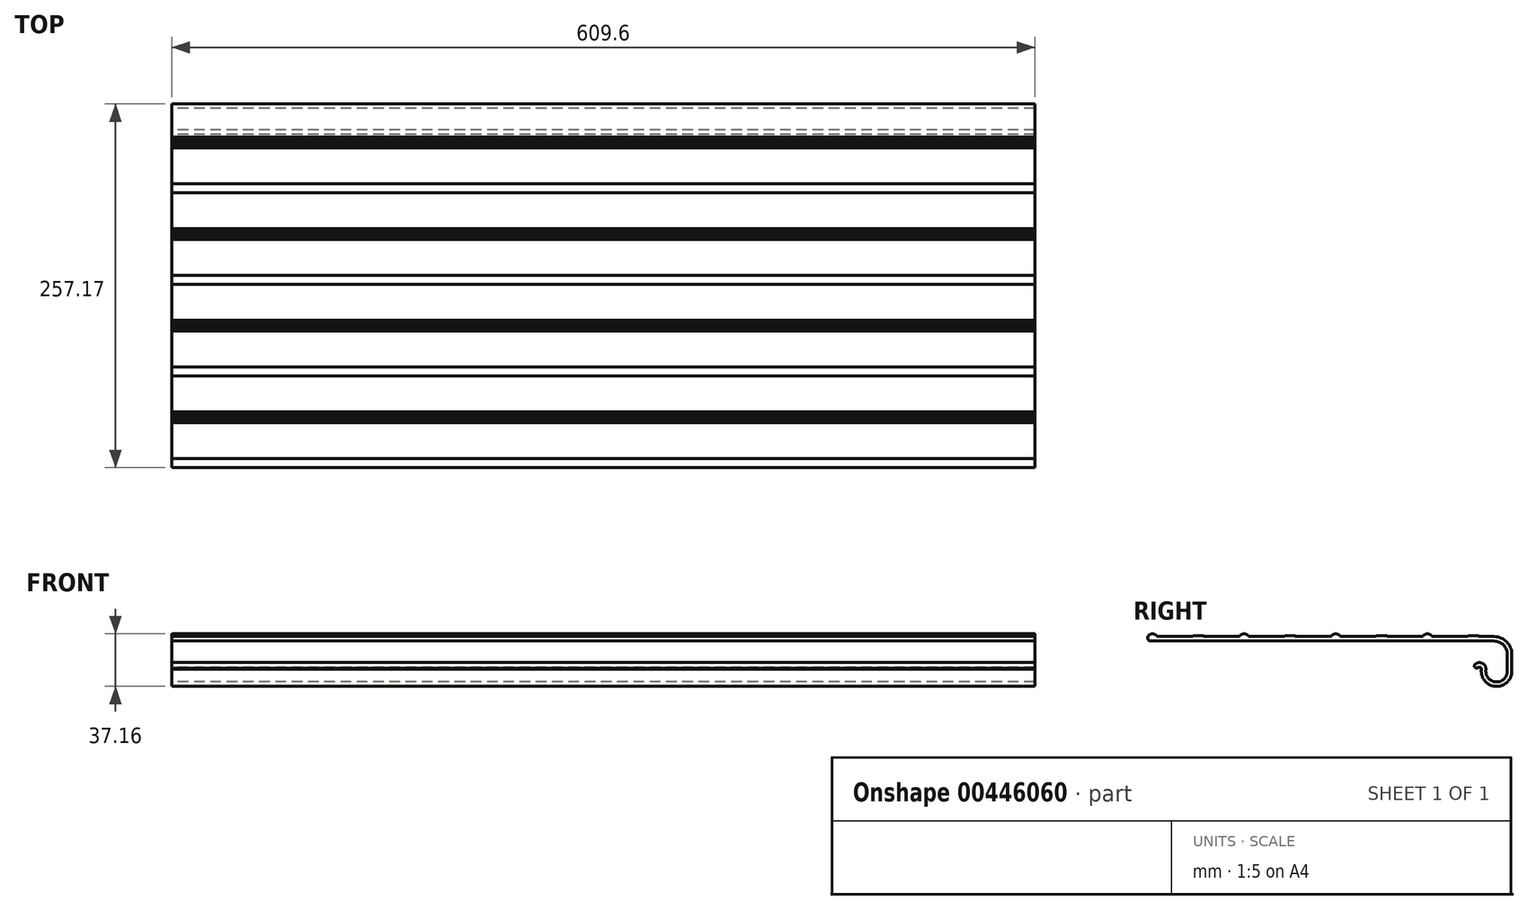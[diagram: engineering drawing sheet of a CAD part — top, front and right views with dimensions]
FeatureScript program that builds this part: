
annotation { "Feature Type Name" : "Feature", "Feature Type Description" : "" }
export const myFeature = defineFeature(function(context is Context, id is Id, definition is map)
    precondition{}
    {
        {
            var Q0;
            Q0=qCreatedBy(makeId("Right.planeOp"),FACE);
            var sketch = newSketch(context, id + "F0", { "sketchPlane" : qUnion([Q0])});
            skLineSegment(sketch, "E0", {"start": v(0, 0) * mm, "end": v(0, -11.72) * mm, "construction": true});
            skLineSegment(sketch, "E1", {"start": v(-9.53, 9.56) * mm, "end": v(-252.41, 9.56) * mm});
            skLineSegment(sketch, "E2.0", {"start": v(-9.53, 12.74) * mm, "end": v(-254, 12.74) * mm});
            skLineSegment(sketch, "E3", {"start": v(-254, 12.74) * mm, "end": v(-254, 11.15) * mm});
            skArc(sketch, "E4", {"start": v(-247.65, 12.74) * mm, "mid": v(-250.83, 14.64) * mm, "end": v(-254, 12.74) * mm});
            skLineSegment(sketch, "E5", {"start": v(0, -11.72) * mm, "end": v(0, 0.04) * mm});
            skLineSegment(sketch, "E6.0", {"start": v(3.18, -11.72) * mm, "end": v(3.17, 0.04) * mm});
            skPoint(sketch, "E7.visualSharp", {"position": v(0, 9.56) * mm});
            skArc(sketch, "E7.filletArc", {"start": v(0, 0.04) * mm, "mid": v(-2.79, 6.77) * mm, "end": v(-9.53, 9.56) * mm});
            skArc(sketch, "E8.filletArc", {"start": v(-15.19, -10.83) * mm, "mid": v(-8.07, -19.33) * mm, "end": v(0, -11.72) * mm});
            skPoint(sketch, "E9.visualSharp", {"position": v(3.18, -23.68) * mm});
            skArc(sketch, "E10", {"start": v(-15.19, -10.83) * mm, "mid": v(-17.6, -6.22) * mm, "end": v(-22.77, -6.79) * mm});
            skArc(sketch, "E11", {"start": v(-22.77, -6.79) * mm, "mid": v(-22.95, -9.02) * mm, "end": v(-20.72, -9.22) * mm});
            skArc(sketch, "E12.0", {"start": v(3.17, 0.04) * mm, "mid": v(-0.54, 9.02) * mm, "end": v(-9.53, 12.74) * mm});
            skArc(sketch, "E13.0", {"start": v(-18.34, -10.46) * mm, "mid": v(-8.25, -22.5) * mm, "end": v(3.18, -11.72) * mm});
            skArc(sketch, "E14", {"start": v(-20.72, -9.22) * mm, "mid": v(-19.12, -9.05) * mm, "end": v(-18.34, -10.46) * mm});
            skLineSegment(sketch, "E15", {"start": v(-222.25, 12.74) * mm, "end": v(-222.25, 13.75) * mm});
            skLineSegment(sketch, "E16", {"start": v(-222.25, 13.75) * mm, "end": v(-221.49, 12.74) * mm});
            skLineSegment(sketch, "E17.1.0.0", {"start": v(-221.49, 13.75) * mm, "end": v(-220.73, 12.74) * mm});
            skLineSegment(sketch, "E17.1.0.1", {"start": v(-221.49, 12.74) * mm, "end": v(-221.49, 13.75) * mm});
            skLineSegment(sketch, "E17.2.0.0", {"start": v(-220.73, 13.75) * mm, "end": v(-219.96, 12.74) * mm});
            skLineSegment(sketch, "E17.2.0.1", {"start": v(-220.73, 12.74) * mm, "end": v(-220.73, 13.75) * mm});
            skLineSegment(sketch, "E17.direction1", {"start": v(-222.25, 12.74) * mm, "end": v(-221.49, 12.74) * mm, "construction": true});
            skLineSegment(sketch, "E18.0.3.0", {"start": v(-219.96, 13.75) * mm, "end": v(-219.2, 12.74) * mm});
            skLineSegment(sketch, "E18.3.3.0", {"start": v(-219.96, 12.74) * mm, "end": v(-219.96, 13.75) * mm});
            skLineSegment(sketch, "E18.0.4.0", {"start": v(-219.2, 13.75) * mm, "end": v(-218.44, 12.74) * mm});
            skLineSegment(sketch, "E18.3.4.0", {"start": v(-219.2, 12.74) * mm, "end": v(-219.2, 13.75) * mm});
            skLineSegment(sketch, "E18.0.5.0", {"start": v(-218.44, 13.75) * mm, "end": v(-217.68, 12.74) * mm});
            skLineSegment(sketch, "E18.3.5.0", {"start": v(-218.44, 12.74) * mm, "end": v(-218.44, 13.75) * mm});
            skLineSegment(sketch, "E18.0.6.0", {"start": v(-217.68, 13.75) * mm, "end": v(-216.92, 12.74) * mm});
            skLineSegment(sketch, "E18.3.6.0", {"start": v(-217.68, 12.74) * mm, "end": v(-217.68, 13.75) * mm});
            skLineSegment(sketch, "E18.0.7.0", {"start": v(-216.92, 13.75) * mm, "end": v(-216.15, 12.74) * mm});
            skLineSegment(sketch, "E18.3.7.0", {"start": v(-216.92, 12.74) * mm, "end": v(-216.92, 13.75) * mm});
            skLineSegment(sketch, "E18.0.8.0", {"start": v(-216.15, 13.75) * mm, "end": v(-215.4, 12.74) * mm});
            skLineSegment(sketch, "E18.3.8.0", {"start": v(-216.15, 12.74) * mm, "end": v(-216.15, 13.75) * mm});
            skLineSegment(sketch, "E18.0.9.0", {"start": v(-215.4, 13.75) * mm, "end": v(-214.63, 12.74) * mm});
            skLineSegment(sketch, "E18.3.9.0", {"start": v(-215.4, 12.74) * mm, "end": v(-215.4, 13.75) * mm});
            skLineSegment(sketch, "E19.1.0.0", {"start": v(-155.96, 12.74) * mm, "end": v(-155.96, 13.75) * mm});
            skLineSegment(sketch, "E19.1.0.1", {"start": v(-155.96, 13.75) * mm, "end": v(-155.2, 12.74) * mm});
            skLineSegment(sketch, "E19.1.0.2", {"start": v(-150.62, 12.74) * mm, "end": v(-150.62, 13.75) * mm});
            skLineSegment(sketch, "E19.1.0.3", {"start": v(-153.67, 12.74) * mm, "end": v(-153.67, 13.75) * mm});
            skLineSegment(sketch, "E19.1.0.4", {"start": v(-155.2, 12.74) * mm, "end": v(-155.2, 13.75) * mm});
            skLineSegment(sketch, "E19.1.0.5", {"start": v(-151.38, 13.75) * mm, "end": v(-150.62, 12.74) * mm});
            skLineSegment(sketch, "E19.1.0.6", {"start": v(-153.67, 13.75) * mm, "end": v(-152.9, 12.74) * mm});
            skLineSegment(sketch, "E19.1.0.7", {"start": v(-157.48, 13.75) * mm, "end": v(-156.72, 12.74) * mm});
            skLineSegment(sketch, "E19.1.0.8", {"start": v(-155.2, 13.75) * mm, "end": v(-154.43, 12.74) * mm});
            skLineSegment(sketch, "E19.1.0.9", {"start": v(-156.72, 13.75) * mm, "end": v(-155.96, 12.74) * mm});
            skLineSegment(sketch, "E19.1.0.10", {"start": v(-154.43, 12.74) * mm, "end": v(-154.43, 13.75) * mm});
            skLineSegment(sketch, "E19.1.0.11", {"start": v(-150.62, 13.75) * mm, "end": v(-149.86, 12.74) * mm});
            skLineSegment(sketch, "E19.1.0.12", {"start": v(-154.43, 13.75) * mm, "end": v(-153.67, 12.74) * mm});
            skLineSegment(sketch, "E19.1.0.13", {"start": v(-152.9, 12.74) * mm, "end": v(-152.9, 13.75) * mm});
            skLineSegment(sketch, "E19.1.0.14", {"start": v(-156.72, 12.74) * mm, "end": v(-156.72, 13.75) * mm});
            skLineSegment(sketch, "E19.1.0.15", {"start": v(-152.9, 13.75) * mm, "end": v(-152.15, 12.74) * mm});
            skLineSegment(sketch, "E19.1.0.16", {"start": v(-152.15, 13.75) * mm, "end": v(-151.38, 12.74) * mm});
            skLineSegment(sketch, "E19.1.0.17", {"start": v(-151.38, 12.74) * mm, "end": v(-151.38, 13.75) * mm});
            skLineSegment(sketch, "E19.1.0.18", {"start": v(-152.15, 12.74) * mm, "end": v(-152.15, 13.75) * mm});
            skLineSegment(sketch, "E19.1.0.19", {"start": v(-157.48, 12.74) * mm, "end": v(-157.48, 13.75) * mm});
            skLineSegment(sketch, "E19.1.0.20", {"start": v(-157.48, 12.74) * mm, "end": v(-156.72, 12.74) * mm, "construction": true});
            skArc(sketch, "E19.1.0.21", {"start": v(-182.88, 12.74) * mm, "mid": v(-186.06, 14.64) * mm, "end": v(-189.23, 12.74) * mm});
            skLineSegment(sketch, "E19.2.0.0", {"start": v(-91.19, 12.74) * mm, "end": v(-91.19, 13.75) * mm});
            skLineSegment(sketch, "E19.2.0.1", {"start": v(-91.19, 13.75) * mm, "end": v(-90.42, 12.74) * mm});
            skLineSegment(sketch, "E19.2.0.2", {"start": v(-85.85, 12.74) * mm, "end": v(-85.85, 13.75) * mm});
            skLineSegment(sketch, "E19.2.0.3", {"start": v(-88.9, 12.74) * mm, "end": v(-88.9, 13.75) * mm});
            skLineSegment(sketch, "E19.2.0.4", {"start": v(-90.42, 12.74) * mm, "end": v(-90.42, 13.75) * mm});
            skLineSegment(sketch, "E19.2.0.5", {"start": v(-86.61, 13.75) * mm, "end": v(-85.85, 12.74) * mm});
            skLineSegment(sketch, "E19.2.0.6", {"start": v(-88.9, 13.75) * mm, "end": v(-88.14, 12.74) * mm});
            skLineSegment(sketch, "E19.2.0.7", {"start": v(-92.7, 13.75) * mm, "end": v(-91.95, 12.74) * mm});
            skLineSegment(sketch, "E19.2.0.8", {"start": v(-90.42, 13.75) * mm, "end": v(-89.66, 12.74) * mm});
            skLineSegment(sketch, "E19.2.0.9", {"start": v(-91.95, 13.75) * mm, "end": v(-91.19, 12.74) * mm});
            skLineSegment(sketch, "E19.2.0.10", {"start": v(-89.66, 12.74) * mm, "end": v(-89.66, 13.75) * mm});
            skLineSegment(sketch, "E19.2.0.11", {"start": v(-85.85, 13.75) * mm, "end": v(-85.1, 12.74) * mm});
            skLineSegment(sketch, "E19.2.0.12", {"start": v(-89.66, 13.75) * mm, "end": v(-88.9, 12.74) * mm});
            skLineSegment(sketch, "E19.2.0.13", {"start": v(-88.14, 12.74) * mm, "end": v(-88.14, 13.75) * mm});
            skLineSegment(sketch, "E19.2.0.14", {"start": v(-91.95, 12.74) * mm, "end": v(-91.95, 13.75) * mm});
            skLineSegment(sketch, "E19.2.0.15", {"start": v(-88.14, 13.75) * mm, "end": v(-87.38, 12.74) * mm});
            skLineSegment(sketch, "E19.2.0.16", {"start": v(-87.38, 13.75) * mm, "end": v(-86.61, 12.74) * mm});
            skLineSegment(sketch, "E19.2.0.17", {"start": v(-86.61, 12.74) * mm, "end": v(-86.61, 13.75) * mm});
            skLineSegment(sketch, "E19.2.0.18", {"start": v(-87.38, 12.74) * mm, "end": v(-87.38, 13.75) * mm});
            skLineSegment(sketch, "E19.2.0.19", {"start": v(-92.71, 12.74) * mm, "end": v(-92.71, 13.75) * mm});
            skLineSegment(sketch, "E19.2.0.20", {"start": v(-92.71, 12.74) * mm, "end": v(-91.95, 12.74) * mm, "construction": true});
            skArc(sketch, "E19.2.0.21", {"start": v(-118.11, 12.74) * mm, "mid": v(-121.29, 14.64) * mm, "end": v(-124.46, 12.74) * mm});
            skLineSegment(sketch, "E19.direction1", {"start": v(-254, 12.74) * mm, "end": v(-189.23, 12.74) * mm, "construction": true});
            skLineSegment(sketch, "E20.0.3.0", {"start": v(-26.42, 12.74) * mm, "end": v(-26.42, 13.75) * mm});
            skLineSegment(sketch, "E20.3.3.0", {"start": v(-26.42, 13.75) * mm, "end": v(-25.65, 12.74) * mm});
            skLineSegment(sketch, "E20.6.3.0", {"start": v(-21.08, 12.74) * mm, "end": v(-21.08, 13.75) * mm});
            skLineSegment(sketch, "E20.9.3.0", {"start": v(-24.13, 12.74) * mm, "end": v(-24.13, 13.75) * mm});
            skLineSegment(sketch, "E20.12.3.0", {"start": v(-25.65, 12.74) * mm, "end": v(-25.65, 13.75) * mm});
            skLineSegment(sketch, "E20.15.3.0", {"start": v(-21.84, 13.75) * mm, "end": v(-21.08, 12.74) * mm});
            skLineSegment(sketch, "E20.18.3.0", {"start": v(-24.13, 13.75) * mm, "end": v(-23.37, 12.74) * mm});
            skLineSegment(sketch, "E20.21.3.0", {"start": v(-27.94, 13.75) * mm, "end": v(-27.18, 12.74) * mm});
            skLineSegment(sketch, "E20.24.3.0", {"start": v(-25.65, 13.75) * mm, "end": v(-24.9, 12.74) * mm});
            skLineSegment(sketch, "E20.27.3.0", {"start": v(-27.18, 13.75) * mm, "end": v(-26.42, 12.74) * mm});
            skLineSegment(sketch, "E20.30.3.0", {"start": v(-24.9, 12.74) * mm, "end": v(-24.9, 13.75) * mm});
            skLineSegment(sketch, "E20.33.3.0", {"start": v(-21.08, 13.75) * mm, "end": v(-20.32, 12.74) * mm});
            skLineSegment(sketch, "E20.36.3.0", {"start": v(-24.9, 13.75) * mm, "end": v(-24.13, 12.74) * mm});
            skLineSegment(sketch, "E20.39.3.0", {"start": v(-23.37, 12.74) * mm, "end": v(-23.37, 13.75) * mm});
            skLineSegment(sketch, "E20.42.3.0", {"start": v(-27.18, 12.74) * mm, "end": v(-27.18, 13.75) * mm});
            skLineSegment(sketch, "E20.45.3.0", {"start": v(-23.37, 13.75) * mm, "end": v(-22.6, 12.74) * mm});
            skLineSegment(sketch, "E20.48.3.0", {"start": v(-22.6, 13.75) * mm, "end": v(-21.84, 12.74) * mm});
            skLineSegment(sketch, "E20.51.3.0", {"start": v(-21.84, 12.74) * mm, "end": v(-21.84, 13.75) * mm});
            skLineSegment(sketch, "E20.54.3.0", {"start": v(-22.6, 12.74) * mm, "end": v(-22.6, 13.75) * mm});
            skLineSegment(sketch, "E20.57.3.0", {"start": v(-27.94, 12.74) * mm, "end": v(-27.94, 13.75) * mm});
            skLineSegment(sketch, "E20.60.3.0", {"start": v(-27.94, 12.74) * mm, "end": v(-27.18, 12.74) * mm, "construction": true});
            skArc(sketch, "E20.63.3.0", {"start": v(-53.34, 12.74) * mm, "mid": v(-56.52, 14.64) * mm, "end": v(-59.7, 12.74) * mm});
            skPoint(sketch, "E21.visualSharp", {"position": v(-254, 9.56) * mm});
            skArc(sketch, "E21.filletArc", {"start": v(-254, 11.15) * mm, "mid": v(-253.54, 10.03) * mm, "end": v(-252.41, 9.56) * mm});
            skSolve(sketch);
        }
        {
            var Q0;
            {var subQ0=sQuery(id+"F0.wireOp",EDGE,"E20.63.3.0");Q0=makeQuery(id+"F0.imprint","IMPRINT",FACE,{"disambiguationData":[TD([[makeQuery(id+"F0.imprint","IMPRINT",EDGE,{"derivedFrom":subQ0}),1.0]])]});}
            var Q1;
            {var subQ0=sQuery(id+"F0.wireOp",EDGE,"E19.2.0.21");Q1=makeQuery(id+"F0.imprint","IMPRINT",FACE,{"disambiguationData":[TD([[makeQuery(id+"F0.imprint","IMPRINT",EDGE,{"derivedFrom":subQ0}),1.0]])]});}
            var Q2;
            Q2=makeQuery(id+"F0.imprint","IMPRINT",FACE,{"disambiguationData":[TD([[makeQuery(id+"F0.imprint","IMPRINT",EDGE,{"derivedFrom":sQuery(id+"F0.wireOp",EDGE,"E1")}),-1.0]])]});
            var Q3;
            {var subQ0=sQuery(id+"F0.wireOp",EDGE,"E4");Q3=makeQuery(id+"F0.imprint","IMPRINT",FACE,{"disambiguationData":[TD([[makeQuery(id+"F0.imprint","IMPRINT",EDGE,{"derivedFrom":subQ0}),1.0]])]});}
            var Q4;
            {var subQ0=sQuery(id+"F0.wireOp",EDGE,"E19.1.0.21");Q4=makeQuery(id+"F0.imprint","IMPRINT",FACE,{"disambiguationData":[TD([[makeQuery(id+"F0.imprint","IMPRINT",EDGE,{"derivedFrom":subQ0}),1.0]])]});}
            var Q5;
            {var subQ0=sQuery(id+"F0.wireOp",EDGE,"E19.2.0.2");Q5=makeQuery(id+"F0.imprint","IMPRINT",FACE,{"disambiguationData":[TD([[makeQuery(id+"F0.imprint","IMPRINT",EDGE,{"derivedFrom":subQ0}),-1.0]])]});}
            var Q6;
            {var subQ0=sQuery(id+"F0.wireOp",EDGE,"E20.6.3.0");Q6=makeQuery(id+"F0.imprint","IMPRINT",FACE,{"disambiguationData":[TD([[makeQuery(id+"F0.imprint","IMPRINT",EDGE,{"derivedFrom":subQ0}),-1.0]])]});}
            var Q7;
            {var subQ0=sQuery(id+"F0.wireOp",EDGE,"E15");Q7=makeQuery(id+"F0.imprint","IMPRINT",FACE,{"disambiguationData":[TD([[makeQuery(id+"F0.imprint","IMPRINT",EDGE,{"derivedFrom":subQ0}),-1.0]])]});}
            var Q8;
            {var subQ0=sQuery(id+"F0.wireOp",EDGE,"E20.15.3.0");Q8=makeQuery(id+"F0.imprint","IMPRINT",FACE,{"disambiguationData":[TD([[makeQuery(id+"F0.imprint","IMPRINT",EDGE,{"derivedFrom":subQ0}),-1.0]])]});}
            var Q9;
            {var subQ0=sQuery(id+"F0.wireOp",EDGE,"E19.1.0.2");Q9=makeQuery(id+"F0.imprint","IMPRINT",FACE,{"disambiguationData":[TD([[makeQuery(id+"F0.imprint","IMPRINT",EDGE,{"derivedFrom":subQ0}),-1.0]])]});}
            var Q10;
            {var subQ0=sQuery(id+"F0.wireOp",EDGE,"E19.1.0.5");Q10=makeQuery(id+"F0.imprint","IMPRINT",FACE,{"disambiguationData":[TD([[makeQuery(id+"F0.imprint","IMPRINT",EDGE,{"derivedFrom":subQ0}),-1.0]])]});}
            var Q11;
            {var subQ2=sQuery(id+"F0.wireOp",EDGE,"E17.1.0.0");Q11=makeQuery(id+"F0.imprint","IMPRINT",FACE,{"disambiguationData":[TD([[makeQuery(id+"F0.imprint","IMPRINT",EDGE,{"derivedFrom":subQ2}),-1.0]])]});}
            var Q12;
            {var subQ0=sQuery(id+"F0.wireOp",EDGE,"E19.2.0.5");Q12=makeQuery(id+"F0.imprint","IMPRINT",FACE,{"disambiguationData":[TD([[makeQuery(id+"F0.imprint","IMPRINT",EDGE,{"derivedFrom":subQ0}),-1.0]])]});}
            var Q13;
            {var subQ0=sQuery(id+"F0.wireOp",EDGE,"E20.0.3.0");Q13=makeQuery(id+"F0.imprint","IMPRINT",FACE,{"disambiguationData":[TD([[makeQuery(id+"F0.imprint","IMPRINT",EDGE,{"derivedFrom":subQ0}),-1.0]])]});}
            var Q14;
            {var subQ0=sQuery(id+"F0.wireOp",EDGE,"E20.27.3.0");Q14=makeQuery(id+"F0.imprint","IMPRINT",FACE,{"disambiguationData":[TD([[makeQuery(id+"F0.imprint","IMPRINT",EDGE,{"derivedFrom":subQ0}),-1.0]])]});}
            var Q15;
            {var subQ0=sQuery(id+"F0.wireOp",EDGE,"E19.1.0.13");Q15=makeQuery(id+"F0.imprint","IMPRINT",FACE,{"disambiguationData":[TD([[makeQuery(id+"F0.imprint","IMPRINT",EDGE,{"derivedFrom":subQ0}),-1.0]])]});}
            var Q16;
            {var subQ0=sQuery(id+"F0.wireOp",EDGE,"E19.1.0.7");Q16=makeQuery(id+"F0.imprint","IMPRINT",FACE,{"disambiguationData":[TD([[makeQuery(id+"F0.imprint","IMPRINT",EDGE,{"derivedFrom":subQ0}),-1.0]])]});}
            var Q17;
            {var subQ2=sQuery(id+"F0.wireOp",EDGE,"E18.0.9.0");Q17=makeQuery(id+"F0.imprint","IMPRINT",FACE,{"disambiguationData":[TD([[makeQuery(id+"F0.imprint","IMPRINT",EDGE,{"derivedFrom":subQ2}),-1.0]])]});}
            var Q18;
            {var subQ0=sQuery(id+"F0.wireOp",EDGE,"E19.2.0.7");Q18=makeQuery(id+"F0.imprint","IMPRINT",FACE,{"disambiguationData":[TD([[makeQuery(id+"F0.imprint","IMPRINT",EDGE,{"derivedFrom":subQ0}),-1.0]])]});}
            var Q19;
            {var subQ2=sQuery(id+"F0.wireOp",EDGE,"E19.2.0.10");Q19=makeQuery(id+"F0.imprint","IMPRINT",FACE,{"disambiguationData":[TD([[makeQuery(id+"F0.imprint","IMPRINT",EDGE,{"derivedFrom":subQ2}),-1.0]])]});}
            var Q20;
            {var subQ0=sQuery(id+"F0.wireOp",EDGE,"E19.1.0.4");Q20=makeQuery(id+"F0.imprint","IMPRINT",FACE,{"disambiguationData":[TD([[makeQuery(id+"F0.imprint","IMPRINT",EDGE,{"derivedFrom":subQ0}),-1.0]])]});}
            var Q21;
            {var subQ0=sQuery(id+"F0.wireOp",EDGE,"E19.1.0.3");Q21=makeQuery(id+"F0.imprint","IMPRINT",FACE,{"disambiguationData":[TD([[makeQuery(id+"F0.imprint","IMPRINT",EDGE,{"derivedFrom":subQ0}),-1.0]])]});}
            var Q22;
            {var subQ0=sQuery(id+"F0.wireOp",EDGE,"E19.2.0.9");Q22=makeQuery(id+"F0.imprint","IMPRINT",FACE,{"disambiguationData":[TD([[makeQuery(id+"F0.imprint","IMPRINT",EDGE,{"derivedFrom":subQ0}),-1.0]])]});}
            var Q23;
            {var subQ2=sQuery(id+"F0.wireOp",EDGE,"E19.2.0.16");Q23=makeQuery(id+"F0.imprint","IMPRINT",FACE,{"disambiguationData":[TD([[makeQuery(id+"F0.imprint","IMPRINT",EDGE,{"derivedFrom":subQ2}),-1.0]])]});}
            var Q24;
            {var subQ0=sQuery(id+"F0.wireOp",EDGE,"E20.9.3.0");Q24=makeQuery(id+"F0.imprint","IMPRINT",FACE,{"disambiguationData":[TD([[makeQuery(id+"F0.imprint","IMPRINT",EDGE,{"derivedFrom":subQ0}),-1.0]])]});}
            var Q25;
            {var subQ0=sQuery(id+"F0.wireOp",EDGE,"E20.21.3.0");Q25=makeQuery(id+"F0.imprint","IMPRINT",FACE,{"disambiguationData":[TD([[makeQuery(id+"F0.imprint","IMPRINT",EDGE,{"derivedFrom":subQ0}),-1.0]])]});}
            var Q26;
            {var subQ0=sQuery(id+"F0.wireOp",EDGE,"E19.2.0.4");Q26=makeQuery(id+"F0.imprint","IMPRINT",FACE,{"disambiguationData":[TD([[makeQuery(id+"F0.imprint","IMPRINT",EDGE,{"derivedFrom":subQ0}),-1.0]])]});}
            var Q27;
            {var subQ0=sQuery(id+"F0.wireOp",EDGE,"E20.39.3.0");Q27=makeQuery(id+"F0.imprint","IMPRINT",FACE,{"disambiguationData":[TD([[makeQuery(id+"F0.imprint","IMPRINT",EDGE,{"derivedFrom":subQ0}),-1.0]])]});}
            var Q28;
            {var subQ2=sQuery(id+"F0.wireOp",EDGE,"E18.0.5.0");Q28=makeQuery(id+"F0.imprint","IMPRINT",FACE,{"disambiguationData":[TD([[makeQuery(id+"F0.imprint","IMPRINT",EDGE,{"derivedFrom":subQ2}),-1.0]])]});}
            var Q29;
            {var subQ2=sQuery(id+"F0.wireOp",EDGE,"E18.0.4.0");Q29=makeQuery(id+"F0.imprint","IMPRINT",FACE,{"disambiguationData":[TD([[makeQuery(id+"F0.imprint","IMPRINT",EDGE,{"derivedFrom":subQ2}),-1.0]])]});}
            var Q30;
            {var subQ2=sQuery(id+"F0.wireOp",EDGE,"E18.0.8.0");Q30=makeQuery(id+"F0.imprint","IMPRINT",FACE,{"disambiguationData":[TD([[makeQuery(id+"F0.imprint","IMPRINT",EDGE,{"derivedFrom":subQ2}),-1.0]])]});}
            var Q31;
            {var subQ0=sQuery(id+"F0.wireOp",EDGE,"E19.1.0.0");Q31=makeQuery(id+"F0.imprint","IMPRINT",FACE,{"disambiguationData":[TD([[makeQuery(id+"F0.imprint","IMPRINT",EDGE,{"derivedFrom":subQ0}),-1.0]])]});}
            var Q32;
            {var subQ2=sQuery(id+"F0.wireOp",EDGE,"E18.0.3.0");Q32=makeQuery(id+"F0.imprint","IMPRINT",FACE,{"disambiguationData":[TD([[makeQuery(id+"F0.imprint","IMPRINT",EDGE,{"derivedFrom":subQ2}),-1.0]])]});}
            var Q33;
            {var subQ0=sQuery(id+"F0.wireOp",EDGE,"E19.2.0.13");Q33=makeQuery(id+"F0.imprint","IMPRINT",FACE,{"disambiguationData":[TD([[makeQuery(id+"F0.imprint","IMPRINT",EDGE,{"derivedFrom":subQ0}),-1.0]])]});}
            var Q34;
            {var subQ0=sQuery(id+"F0.wireOp",EDGE,"E19.2.0.3");Q34=makeQuery(id+"F0.imprint","IMPRINT",FACE,{"disambiguationData":[TD([[makeQuery(id+"F0.imprint","IMPRINT",EDGE,{"derivedFrom":subQ0}),-1.0]])]});}
            var Q35;
            {var subQ2=sQuery(id+"F0.wireOp",EDGE,"E20.30.3.0");Q35=makeQuery(id+"F0.imprint","IMPRINT",FACE,{"disambiguationData":[TD([[makeQuery(id+"F0.imprint","IMPRINT",EDGE,{"derivedFrom":subQ2}),-1.0]])]});}
            var Q36;
            {var subQ2=sQuery(id+"F0.wireOp",EDGE,"E19.1.0.16");Q36=makeQuery(id+"F0.imprint","IMPRINT",FACE,{"disambiguationData":[TD([[makeQuery(id+"F0.imprint","IMPRINT",EDGE,{"derivedFrom":subQ2}),-1.0]])]});}
            var Q37;
            {var subQ2=sQuery(id+"F0.wireOp",EDGE,"E17.2.0.0");Q37=makeQuery(id+"F0.imprint","IMPRINT",FACE,{"disambiguationData":[TD([[makeQuery(id+"F0.imprint","IMPRINT",EDGE,{"derivedFrom":subQ2}),-1.0]])]});}
            var Q38;
            {var subQ2=sQuery(id+"F0.wireOp",EDGE,"E18.0.7.0");Q38=makeQuery(id+"F0.imprint","IMPRINT",FACE,{"disambiguationData":[TD([[makeQuery(id+"F0.imprint","IMPRINT",EDGE,{"derivedFrom":subQ2}),-1.0]])]});}
            var Q39;
            {var subQ0=sQuery(id+"F0.wireOp",EDGE,"E19.1.0.9");Q39=makeQuery(id+"F0.imprint","IMPRINT",FACE,{"disambiguationData":[TD([[makeQuery(id+"F0.imprint","IMPRINT",EDGE,{"derivedFrom":subQ0}),-1.0]])]});}
            var Q40;
            {var subQ2=sQuery(id+"F0.wireOp",EDGE,"E19.1.0.10");Q40=makeQuery(id+"F0.imprint","IMPRINT",FACE,{"disambiguationData":[TD([[makeQuery(id+"F0.imprint","IMPRINT",EDGE,{"derivedFrom":subQ2}),-1.0]])]});}
            var Q41;
            {var subQ2=sQuery(id+"F0.wireOp",EDGE,"E18.0.6.0");Q41=makeQuery(id+"F0.imprint","IMPRINT",FACE,{"disambiguationData":[TD([[makeQuery(id+"F0.imprint","IMPRINT",EDGE,{"derivedFrom":subQ2}),-1.0]])]});}
            var Q42;
            {var subQ0=sQuery(id+"F0.wireOp",EDGE,"E20.12.3.0");Q42=makeQuery(id+"F0.imprint","IMPRINT",FACE,{"disambiguationData":[TD([[makeQuery(id+"F0.imprint","IMPRINT",EDGE,{"derivedFrom":subQ0}),-1.0]])]});}
            var Q43;
            {var subQ2=sQuery(id+"F0.wireOp",EDGE,"E20.48.3.0");Q43=makeQuery(id+"F0.imprint","IMPRINT",FACE,{"disambiguationData":[TD([[makeQuery(id+"F0.imprint","IMPRINT",EDGE,{"derivedFrom":subQ2}),-1.0]])]});}
            var Q44;
            {var subQ0=sQuery(id+"F0.wireOp",EDGE,"E19.2.0.0");Q44=makeQuery(id+"F0.imprint","IMPRINT",FACE,{"disambiguationData":[TD([[makeQuery(id+"F0.imprint","IMPRINT",EDGE,{"derivedFrom":subQ0}),-1.0]])]});}
            extrude(context, id + "F1", {"entities" : qUnion([Q0, Q1, Q2, Q3, Q4, Q5, Q6, Q7, Q8, Q9, Q10, Q11, Q12, Q13, Q14, Q15, Q16, Q17, Q18, Q19, Q20, Q21, Q22, Q23, Q24, Q25, Q26, Q27, Q28, Q29, Q30, Q31, Q32, Q33, Q34, Q35, Q36, Q37, Q38, Q39, Q40, Q41, Q42, Q43, Q44]), "depth" : 609.6 * mm, "offsetDistance" : 25.4 * mm});
        }
    });
